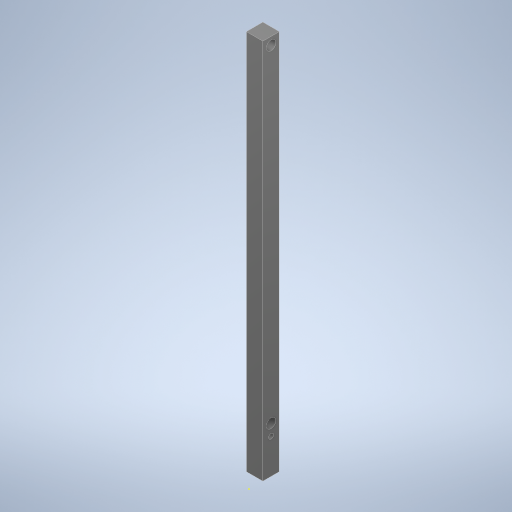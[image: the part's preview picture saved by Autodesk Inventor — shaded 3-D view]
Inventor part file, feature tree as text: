
AUTODESK INVENTOR PART (.ipt)
format: ipt  version: 2024 (Build 280153000, 153)  size: 775,168 bytes
history: native  units: in
note: dims shown in document units (in); Inventor stores cm internally (conversion verified against a paired STEP export)
features: sketch x5, hole x2, extrude x2, imported_body x1
ambient origin geometry x8: Origin, YZ Plane, XZ Plane, XY Plane, X Axis, Y Axis, Z Axis, Center Point
bodies: Solid1 (feature_tree)
feature tree (10):
  imported_body  "Base1"
  hole  "Hole1"  [1 undecoded]
  sketch  "Sketch2"  dims[d2=0.0625in d3=0.75in d4=0.375in d5=0.25in d6=0.5635in d7=1.0in d8=0.8108in d9=0.208in d10=0.0in]
  extrude  "Extrusion1"  Depth=0.208in TaperAngle=0.0deg
  extrude  "Extrusion2"  Depth=0.0984in
  hole  "Hole2"  [1 undecoded]
  sketch  "Sketch1"  dims[d0=0.407in d1=0.0312in]
  sketch  "Sketch3"  dims[d11=0.483in d12=0.0in d13=0.0984in]
  sketch  "Sketch4"  dims[d14=4.2323in d15=0.12in]
  sketch  "Sketch5"  dims[d16=0.12in d17=0.12in d18=0.75in d19=0.375in d20=0.25in d21=0.5635in d22=1.0in d23=0.8108in d24=0.75in d25=0.8108in d26=0.0625in d27=0.75in d28=0.375in]
note: 2 required parameter values undecoded (feature->parameter linkage not recoverable at this tier; creation-order binding heuristic only, values carry confidence <= 0.55)
